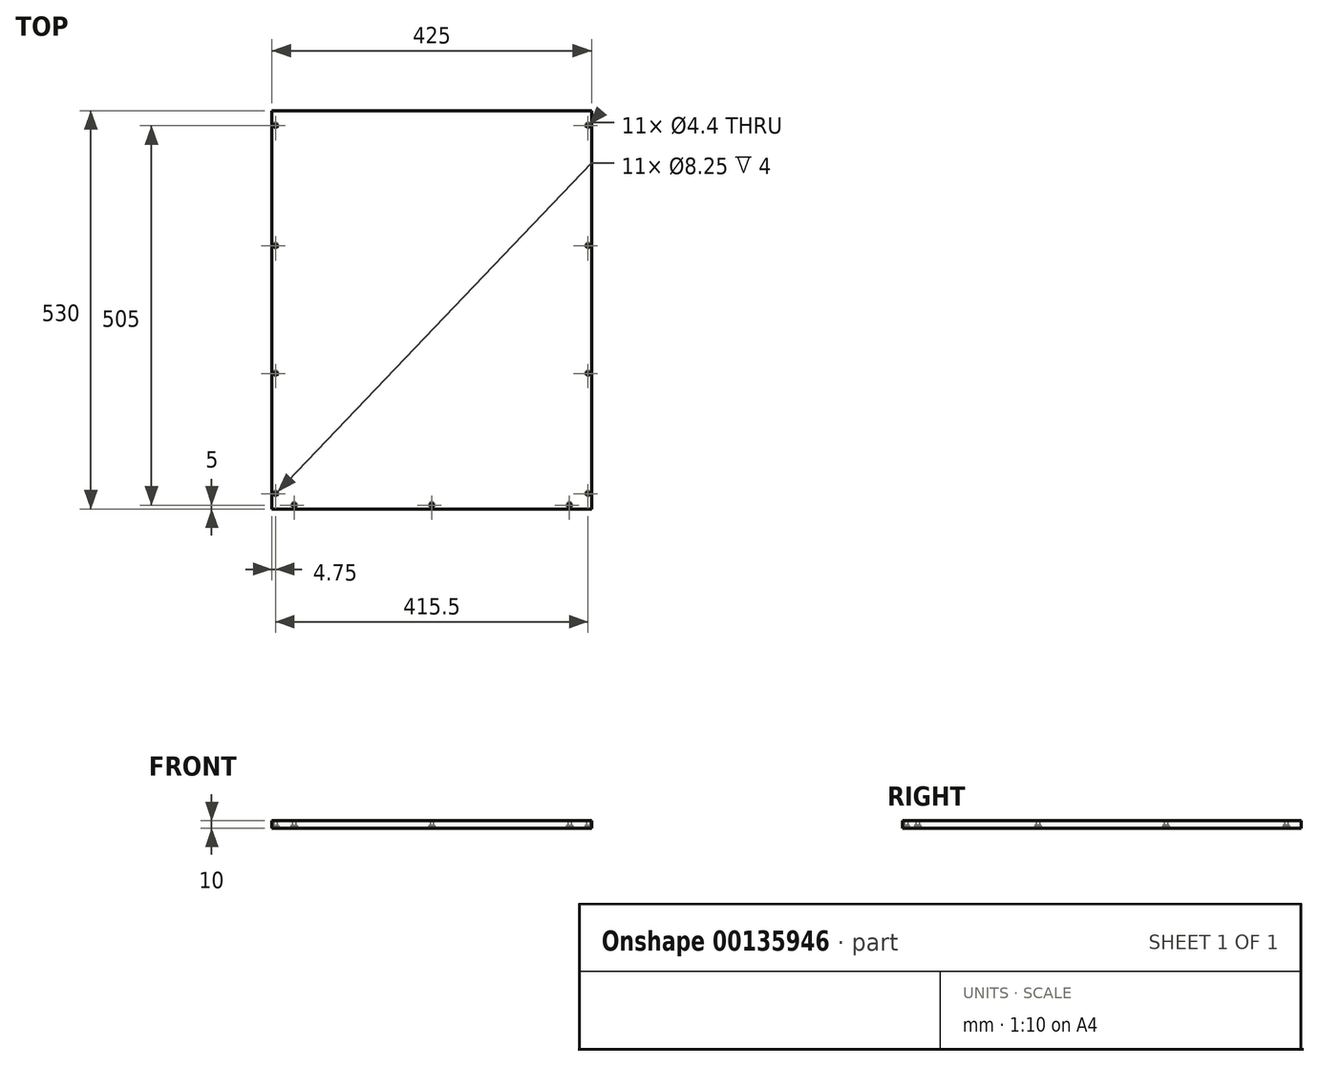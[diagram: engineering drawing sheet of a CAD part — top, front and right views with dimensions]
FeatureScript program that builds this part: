
annotation { "Feature Type Name" : "Feature", "Feature Type Description" : "" }
export const myFeature = defineFeature(function(context is Context, id is Id, definition is map)
    precondition{}
    {
        {
            var Q0;
            Q0=qCreatedBy(makeId("Top.planeOp"),FACE);
            var sketch = newSketch(context, id + "F0", { "sketchPlane" : qUnion([Q0])});
            skLineSegment(sketch, "E0.bottom", {"start": v(212.5, -265) * mm, "end": v(-212.5, -265) * mm});
            skLineSegment(sketch, "E0.top", {"start": v(212.5, 265) * mm, "end": v(-212.5, 265) * mm});
            skLineSegment(sketch, "E0.left", {"start": v(212.5, -265) * mm, "end": v(212.5, 265) * mm});
            skLineSegment(sketch, "E0.right", {"start": v(-212.5, -265) * mm, "end": v(-212.5, 265) * mm});
            skPoint(sketch, "E0.middle", {"position": v(0, 0) * mm});
            skLineSegment(sketch, "E1.top", {"start": v(81.24, -196.03) * mm, "end": v(129.3, -196.03) * mm});
            skSolve(sketch);
        }
        {
            var Q0;
            Q0=qSketchRegion(id+"F0",true);
            extrude(context, id + "F1", {"entities" : qUnion([Q0]), "endBound" : BoundingType.SYMMETRIC, "depth" : 10 * mm});
        }
        {
            var Q0;
            Q0=makeQuery(id+"F1.opExtrude","CAP_FACE",FACE,{"disambiguationData":[OSD([sQuery(id+"F0.wireOp",EDGE,"E0.bottom"),sQuery(id+"F0.wireOp",EDGE,"E0.top"),sQuery(id+"F0.wireOp",EDGE,"E0.left"),sQuery(id+"F0.wireOp",EDGE,"E0.right")])],"isStart":true});
            var sketch = newSketch(context, id + "F2", { "sketchPlane" : qUnion([Q0])});
            skCircle(sketch, "E2", {"center": v(-207.75, 245) * mm, "radius": 2 * mm});
            skCircle(sketch, "E3", {"center": v(-207.75, 85) * mm, "radius": 2 * mm});
            skCircle(sketch, "E4.MirrorC", {"center": v(-207.75, -85) * mm, "radius": 2 * mm});
            skCircle(sketch, "E5.MirrorC", {"center": v(-207.75, -245) * mm, "radius": 2 * mm});
            skCircle(sketch, "E6.MirrorC", {"center": v(207.75, 245) * mm, "radius": 2 * mm});
            skCircle(sketch, "E7.MirrorC", {"center": v(207.75, 85) * mm, "radius": 2 * mm});
            skCircle(sketch, "E8.MirrorC", {"center": v(207.75, -85) * mm, "radius": 2 * mm});
            skCircle(sketch, "E9.MirrorC", {"center": v(207.75, -245) * mm, "radius": 2 * mm});
            skCircle(sketch, "E10", {"center": v(-183, 260) * mm, "radius": 2 * mm});
            skCircle(sketch, "E11.1.0.0", {"center": v(0, 260) * mm, "radius": 2 * mm});
            skCircle(sketch, "E11.2.0.0", {"center": v(183, 260) * mm, "radius": 2 * mm});
            skLineSegment(sketch, "E11.direction1", {"start": v(-183, 260) * mm, "end": v(0, 260) * mm, "construction": true});
            skSolve(sketch);
        }
        {
            var Q0;
            Q0=sQuery(id+"F2.wireOp",VERTEX,"E2.center");
            var Q1;
            Q1=sQuery(id+"F2.wireOp",VERTEX,"E3.center");
            var Q2;
            Q2=sQuery(id+"F2.wireOp",VERTEX,"E4.MirrorC.center");
            var Q3;
            Q3=sQuery(id+"F2.wireOp",VERTEX,"E5.MirrorC.center");
            var Q4;
            Q4=sQuery(id+"F2.wireOp",VERTEX,"E9.MirrorC.center");
            var Q5;
            Q5=sQuery(id+"F2.wireOp",VERTEX,"E8.MirrorC.center");
            var Q6;
            Q6=sQuery(id+"F2.wireOp",VERTEX,"E7.MirrorC.center");
            var Q7;
            Q7=sQuery(id+"F2.wireOp",VERTEX,"E6.MirrorC.center");
            var Q8;
            Q8=sQuery(id+"F2.wireOp",VERTEX,"kkFZym1l-DYRr-YCzm-noe1-ySgtALnpHWht.center");
            var Q9;
            Q9=sQuery(id+"F2.wireOp",VERTEX,"WoDvKdXF-PdJz-WFzz-Z4uX-elENKUMFdGKx.center");
            var Q10;
            Q10=sQuery(id+"F2.wireOp",VERTEX,"axoy2mSQ-Yy3T-ROeZ-40XW-cdWlI4RzoubP.center");
            var Q11;
            Q11=sQuery(id+"F2.wireOp",VERTEX,"Gf7lKQ4c-8bLx-3h7W-wmy7-qyMdfDCTACcy.center");
            var Q12;
            Q12=sQuery(id+"F2.wireOp",VERTEX,"afeb9733-eb6e-4099-b4cc-138f5442d24a0.MirrorC.center");
            var Q13;
            Q13=sQuery(id+"F2.wireOp",VERTEX,"5a1a8710-edd7-43ff-9459-da1546c242ab0.MirrorC.center");
            var Q14;
            Q14=sQuery(id+"F2.wireOp",VERTEX,"c1e0f906-5fed-4c0f-b8fc-75f51ee2fa860.MirrorC.center");
            var Q15;
            Q15=sQuery(id+"F2.wireOp",VERTEX,"86eb54a1-4769-462b-b598-50202e1166000.MirrorC.center");
            var Q16;
            Q16=sQuery(id+"F2.wireOp",VERTEX,"6J1cC2zl-gnNa-lyWi-kusl-kWZGhb2Tm6Yi.center");
            var Q17;
            Q17=sQuery(id+"F2.wireOp",VERTEX,"2Pyidt3F-xQNL-qOz5-DrPg-jibaZAFIGgOY.center");
            var Q18;
            Q18=sQuery(id+"F2.wireOp",VERTEX,"3b745f28-dec8-4eaf-b7a0-753a52fb6e040.MirrorC.center");
            var Q19;
            Q19=sQuery(id+"F2.wireOp",VERTEX,"65bc9fd0-061f-4973-9c23-7b2eaf92318f0.MirrorC.center");
            var Q20;
            Q20=sQuery(id+"F2.wireOp",VERTEX,"YBY1wmDJ-lx34-VKfA-q6n2-4bksJfFcZfsM.center");
            var Q21;
            Q21=sQuery(id+"F2.wireOp",VERTEX,"80bfd170-c0ba-45f0-bb06-3c2dd546f4050.MirrorC.center");
            var Q22;
            Q22=sQuery(id+"F2.wireOp",VERTEX,"ad8630ff-44f7-4325-af5a-6699211c33040.MirrorC.center");
            var Q23;
            Q23=sQuery(id+"F2.wireOp",VERTEX,"1TXsvVGW-e218-WKv5-m2LJ-yHWH1ysALa7e.center");
            var Q24;
            Q24=sQuery(id+"F2.wireOp",VERTEX,"25ckQPhh-FslX-xcYU-JyPb-b9t6GhTTHOzC.center");
            var Q25;
            Q25=sQuery(id+"F2.wireOp",VERTEX,"f6d9d3b5-e9be-4bde-a98f-a08746848e9f0.MirrorC.center");
            var Q26;
            Q26=sQuery(id+"F2.wireOp",VERTEX,"e25a9e91-0994-4afc-bc73-87788ebad6020.MirrorC.center");
            var Q27;
            Q27=sQuery(id+"F2.wireOp",VERTEX,"E10.center");
            var Q28;
            Q28=sQuery(id+"F2.wireOp",VERTEX,"E11.direction1.end");
            var Q29;
            Q29=sQuery(id+"F2.wireOp",VERTEX,"E11.2.0.0.center");
            var Q30;
            Q30=makeQuery(id+"F1.opExtrude","SWEPT_BODY",BODY,{"disambiguationData":[OSD([sQuery(id+"F0.wireOp",EDGE,"E0.bottom"),sQuery(id+"F0.wireOp",EDGE,"E0.top"),sQuery(id+"F0.wireOp",EDGE,"E0.left"),sQuery(id+"F0.wireOp",EDGE,"E0.right")])]});
            hole(context, id + "F3", {"style" : HoleStyle.C_BORE, "endStyle" : HoleEndStyle.THROUGH, "standardTappedOrClearance" : lookupTablePath({ "standard" : "ISO", "fit" : "Normal", "size" : "M4", "type" : "Clearance" }), "standardBlindInLast" : lookupTablePath({ "fit" : "Standard", "standard" : "ISO", "size" : "M4", "type" : "Clearance" }), "holeDiameter" : 4.4 * mm, "cBoreDiameter" : 8.25 * mm, "cBoreDepth" : 4 * mm, "locations" : qUnion([Q0, Q1, Q2, Q3, Q4, Q5, Q6, Q7, Q8, Q9, Q10, Q11, Q12, Q13, Q14, Q15, Q16, Q17, Q18, Q19, Q20, Q21, Q22, Q23, Q24, Q25, Q26, Q27, Q28, Q29]), "scope" : qUnion([Q30]), "isTappedThrough" : true});
        }
    });
